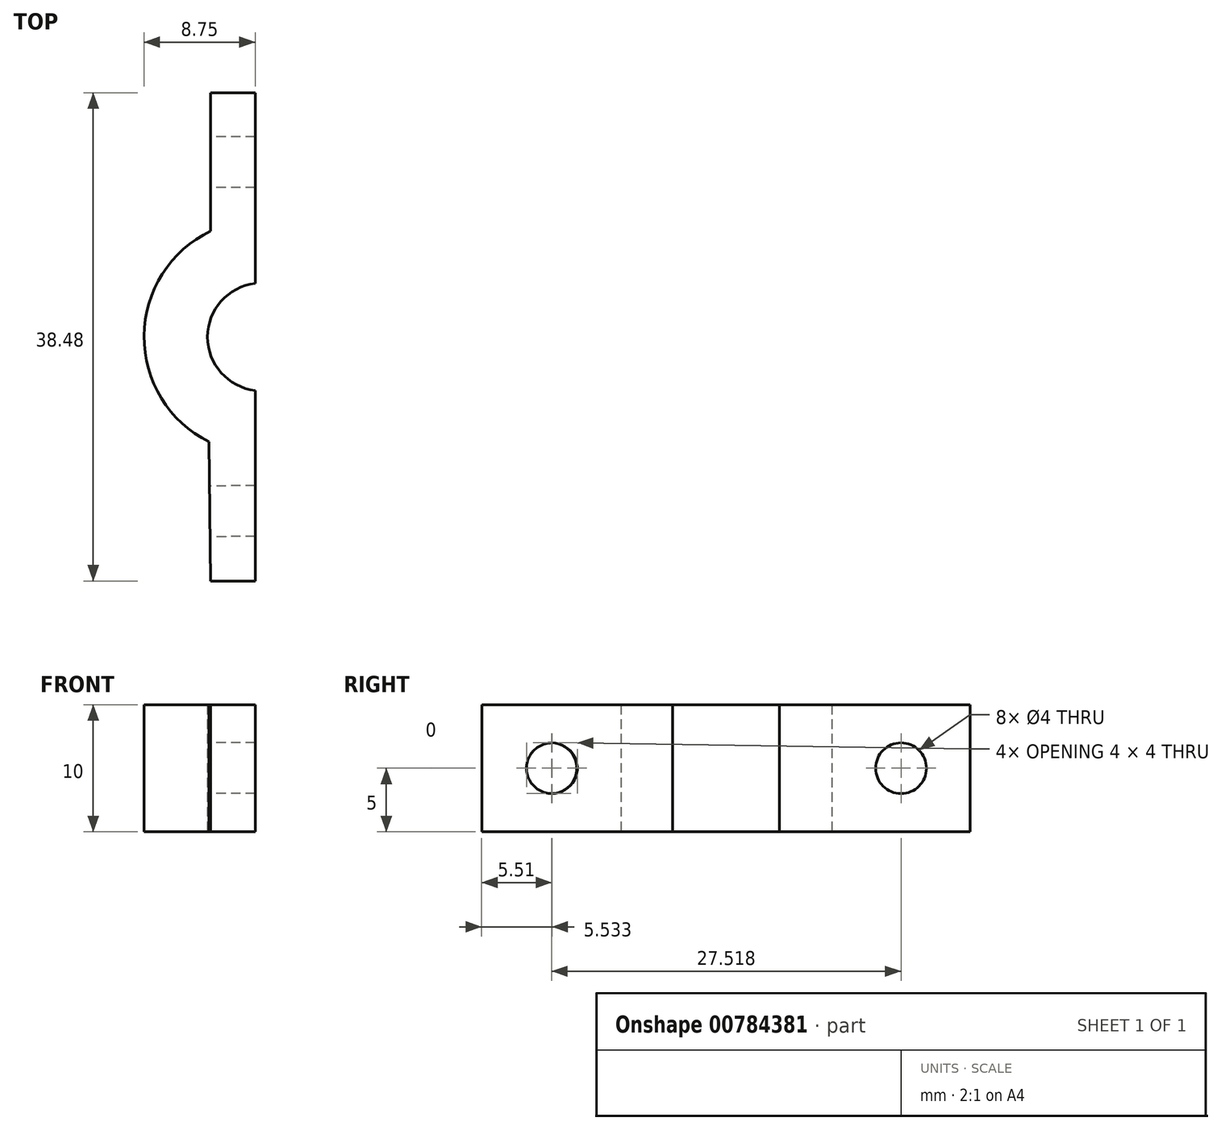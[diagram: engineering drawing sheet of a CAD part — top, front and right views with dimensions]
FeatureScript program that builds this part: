
annotation { "Feature Type Name" : "Feature", "Feature Type Description" : "" }
export const myFeature = defineFeature(function(context is Context, id is Id, definition is map)
    precondition{}
    {
        {
            var Q0;
            Q0=qCreatedBy(makeId("Top.planeOp"),FACE);
            var sketch = newSketch(context, id + "F0", { "sketchPlane" : qUnion([Q0])});
            skArc(sketch, "E0", {"start": v(-0.5, 4.22) * mm, "mid": v(-4.25, 0) * mm, "end": v(-0.5, -4.22) * mm});
            skArc(sketch, "E1", {"start": v(-4, 8.34) * mm, "mid": v(-9.25, 0.08) * mm, "end": v(-4.14, -8.27) * mm});
            skLineSegment(sketch, "E2", {"start": v(-0.5, 9.24) * mm, "end": v(-0.5, 19.24) * mm});
            skLineSegment(sketch, "E3", {"start": v(-0.5, 19.24) * mm, "end": v(-4, 19.24) * mm});
            skLineSegment(sketch, "E4", {"start": v(-4, 19.24) * mm, "end": v(-4, 8.34) * mm});
            skLineSegment(sketch, "E5", {"start": v(-0.5, -9.24) * mm, "end": v(-0.5, -19.24) * mm});
            skLineSegment(sketch, "E6", {"start": v(-0.5, -19.24) * mm, "end": v(-4, -19.24) * mm});
            skLineSegment(sketch, "E7", {"start": v(-4, -19.24) * mm, "end": v(-4.14, -8.27) * mm});
            skLineSegment(sketch, "E8", {"start": v(-0.5, 9.24) * mm, "end": v(-0.5, 4.22) * mm});
            skLineSegment(sketch, "E9.trimOffspring", {"start": v(-0.5, -4.22) * mm, "end": v(-0.5, -9.24) * mm});
            skSolve(sketch);
        }
        {
            var Q0;
            Q0=makeQuery(id+"F0.imprint","IMPRINT",FACE,{"disambiguationData":[TD([[makeQuery(id+"F0.imprint","IMPRINT",EDGE,{"derivedFrom":sQuery(id+"F0.wireOp",EDGE,"E0")}),-1.0]])]});
            extrude(context, id + "F1", {"entities" : qUnion([Q0]), "depth" : 10 * mm, "offsetDistance" : 25 * mm});
        }
        {
            var Q0;
            Q0=makeQuery(id+"F1.opExtrude","SWEPT_FACE",FACE,{"disambiguationData":[OSD([sQuery(id+"F0.wireOp",EDGE,"E4")])]});
            var sketch = newSketch(context, id + "F2", { "sketchPlane" : qUnion([Q0])});
            skCircle(sketch, "E10", {"center": v(-13.79, 5) * mm, "radius": 2 * mm});
            skPoint(sketch, "E10.centerSnap0", {"position": v(-19.24, 5) * mm});
            skPoint(sketch, "E10.centerSnap1", {"position": v(-13.79, 10) * mm});
            skCircle(sketch, "E11", {"center": v(13.71, 5) * mm, "radius": 2 * mm});
            skSolve(sketch);
        }
        {
            var Q0;
            Q0=makeQuery(id+"F2.imprint","IMPRINT",FACE,{"disambiguationData":[TD([[makeQuery(id+"F2.imprint","IMPRINT",EDGE,{"derivedFrom":sQuery(id+"F2.wireOp",EDGE,"E10")}),1.0]])]});
            var Q1;
            Q1=sQuery(id+"F2.wireOp",EDGE,"E11");
            extrude(context, id + "F3", {"entities" : qUnion([Q0]), "operationType" : NewBodyOperationType.REMOVE, "surfaceEntities" : qUnion([Q1]), "oppositeDirection" : true, "depth" : 25 * mm, "offsetDistance" : 25 * mm});
        }
        {
            var Q0;
            Q0=makeQuery(id+"F1.opExtrude","SWEPT_FACE",FACE,{"disambiguationData":[OSD([sQuery(id+"F0.wireOp",EDGE,"E7")])]});
            var sketch = newSketch(context, id + "F4", { "sketchPlane" : qUnion([Q0])});
            skCircle(sketch, "E12", {"center": v(13.7, 5) * mm, "radius": 2 * mm});
            skPoint(sketch, "E12.centerSnap0", {"position": v(19.18, 5) * mm});
            skPoint(sketch, "E12.centerSnap1", {"position": v(13.7, 10) * mm});
            skSolve(sketch);
        }
        {
            var Q0;
            Q0=makeQuery(id+"F4.imprint","IMPRINT",FACE,{"disambiguationData":[TD([[makeQuery(id+"F4.imprint","IMPRINT",EDGE,{"derivedFrom":sQuery(id+"F4.wireOp",EDGE,"E12")}),1.0]])]});
            extrude(context, id + "F5", {"entities" : qUnion([Q0]), "operationType" : NewBodyOperationType.REMOVE, "oppositeDirection" : true, "depth" : 25 * mm, "offsetDistance" : 25 * mm});
        }
    });
